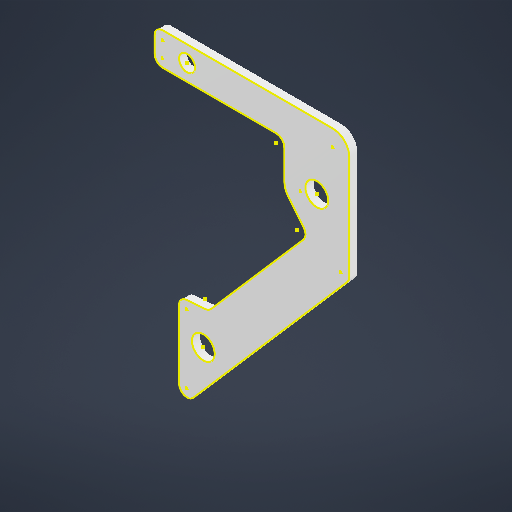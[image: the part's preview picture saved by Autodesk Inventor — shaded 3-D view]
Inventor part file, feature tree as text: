
AUTODESK INVENTOR PART (.ipt)
format: ipt  version: 2025.2 (Build 292293000, 293)  size: 283,136 bytes
history: native  units: in
note: dims shown in document units (in); Inventor stores cm internally (conversion verified against a paired STEP export)
features: other x3, sketch x1
ambient origin geometry x8: Origin, YZ Plane, XZ Plane, XY Plane, X Axis, Y Axis, Z Axis, Center Point
bodies: Solid1 (feature_tree)
feature tree (4):
  sketch  "Sketch1"
  other  "A-Side Definition"
  other  "Part 1"
  other  "Definition1"
